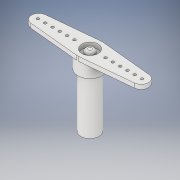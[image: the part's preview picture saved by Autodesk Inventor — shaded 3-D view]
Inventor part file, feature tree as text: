
AUTODESK INVENTOR PART (.ipt)
format: ipt  version: 2018 (Build 220112000, 112)  size: 165,888 bytes
history: native  units: in
note: dims shown in document units (in); Inventor stores cm internally (conversion verified against a paired STEP export)
features: extrude x6, sketch x6, fillet x1, mirror x1
ambient origin geometry x8: Origin, YZ Plane, XZ Plane, XY Plane, X Axis, Y Axis, Z Axis, Center Point
bodies: Solid1 (feature_tree)
feature tree (14):
  extrude  "Extrusion1"  Depth=0.374in TaperAngle=0.0deg
  extrude  "Extrusion2"  Depth=0.2638in
  extrude  "Extrusion3"  Depth=0.0787in
  extrude  "Extrusion4"  Depth=0.0335in
  extrude  "Extrusion5"  Depth=0.1378in TaperAngle=0.0deg
  fillet  "Fillet1"  Radius=0.1772in
  extrude  "Extrusion6"  Depth=0.0984in
  mirror  "Mirror1"
  sketch  "Sketch1"  dims[d0=0.1969in d1=0.374in d2=0.3937in d3=0.0in d4=0.0in]
  sketch  "Sketch2"  dims[d5=0.6299in d6=0.2638in]
  sketch  "Sketch3"  dims[d7=0.1575in d8=0.0787in]
  sketch  "Sketch4"  dims[d9=0.0335in d10=0.0335in d11=0.0335in]
  sketch  "Sketch5"  dims[d12=0.0472in d13=0.0in d14=0.1378in d15=0.0in d16=0.1772in]
  sketch  "Sketch6"  dims[d17=0.0492in d18=0.0in d19=0.0984in d20=0.0492in d21=0.0in d22=0.0291in d23=0.0295in d24=0.1673in d25=2.3622in d27=0.0787in d28=0.3937in d30=0.3937in d32=0.1117in d33=0.0in]
